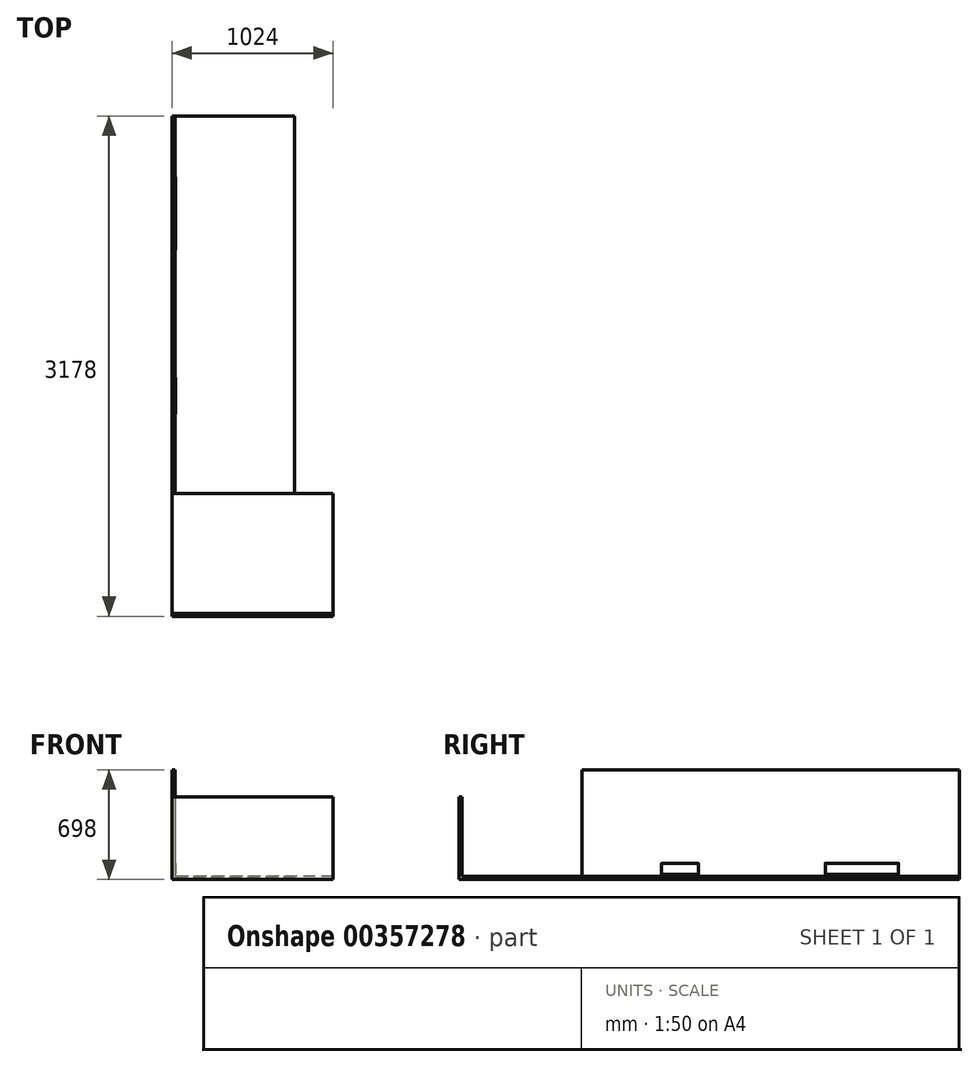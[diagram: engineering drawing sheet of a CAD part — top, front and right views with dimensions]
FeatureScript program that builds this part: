
annotation { "Feature Type Name" : "Feature", "Feature Type Description" : "" }
export const myFeature = defineFeature(function(context is Context, id is Id, definition is map)
    precondition{}
    {
        {
            var Q0;
            Q0=qCreatedBy(makeId("Front.planeOp"),FACE);
            var sketch = newSketch(context, id + "F0", { "sketchPlane" : qUnion([Q0])});
            skLineSegment(sketch, "E0.top", {"start": v(-380, -339.5) * mm, "end": v(380, -339.5) * mm});
            skLineSegment(sketch, "E0.left", {"start": v(-380, 339.5) * mm, "end": v(-380, -339.5) * mm});
            skPoint(sketch, "E0.middle", {"position": v(0, 0) * mm});
            skPoint(sketch, "E0.right.start.orphan", {"position": v(380, 339.5) * mm});
            skLineSegment(sketch, "E1", {"start": v(-380, 339.5) * mm, "end": v(380, -339.5) * mm, "construction": true});
            skLineSegment(sketch, "E2.0", {"start": v(-399, -358.5) * mm, "end": v(380.02, -358.5) * mm});
            skLineSegment(sketch, "E2.1", {"start": v(-399, 339.48) * mm, "end": v(-399, -358.5) * mm});
            skLineSegment(sketch, "E3", {"start": v(-380, 339.5) * mm, "end": v(-399, 339.48) * mm});
            skLineSegment(sketch, "E4", {"start": v(380.02, -358.5) * mm, "end": v(380, -339.5) * mm});
            skSolve(sketch);
        }
        {
            var Q0;
            Q0 = qSketchRegion(id + "F0", true);
            extrude(context, id + "F1", {"entities" : qUnion([Q0]), "endBound" : BoundingType.SYMMETRIC, "depth" : 2398 * mm});
        }
        {
            var Q0;
            Q0=makeQuery(id+"F1.opExtrude","SWEPT_FACE",FACE,{"disambiguationData":[OSD([sQuery(id+"F0.wireOp",EDGE,"E0.left")])]});
            var sketch = newSketch(context, id + "F2", { "sketchPlane" : qUnion([Q0])});
            skLineSegment(sketch, "E5.bottom", {"start": v(-694, -254.5) * mm, "end": v(-461, -254.5) * mm});
            skLineSegment(sketch, "E5.top", {"start": v(-694, -324.5) * mm, "end": v(-461, -324.5) * mm});
            skLineSegment(sketch, "E5.left", {"start": v(-694, -254.5) * mm, "end": v(-694, -324.5) * mm});
            skLineSegment(sketch, "E5.right", {"start": v(-461, -254.5) * mm, "end": v(-461, -324.5) * mm});
            skLineSegment(sketch, "E6.bottom", {"start": v(811, -254.5) * mm, "end": v(346, -254.5) * mm});
            skLineSegment(sketch, "E6.top", {"start": v(811, -324.5) * mm, "end": v(346, -324.5) * mm});
            skLineSegment(sketch, "E6.left", {"start": v(811, -254.5) * mm, "end": v(811, -324.5) * mm});
            skLineSegment(sketch, "E6.right", {"start": v(346, -254.5) * mm, "end": v(346, -324.5) * mm});
            skSolve(sketch);
        }
        {
            var Q0;
            Q0 = qSketchRegion(id + "F2", true);
            extrude(context, id + "F3", {"entities" : qUnion([Q0]), "operationType" : NewBodyOperationType.ADD, "depth" : 5 * mm});
        }
        {
            var Q0;
            Q0=makeQuery(id+"F3.opExtrude","CAP_FACE",FACE,{"disambiguationData":[OSD([sQuery(id+"F2.wireOp",EDGE,"E5.bottom"),sQuery(id+"F2.wireOp",EDGE,"E5.top"),sQuery(id+"F2.wireOp",EDGE,"E5.left"),sQuery(id+"F2.wireOp",EDGE,"E5.right")])],"isStart":false});
            var Q1;
            Q1=makeQuery(id+"F3.opExtrude","CAP_FACE",FACE,{"disambiguationData":[OSD([sQuery(id+"F2.wireOp",EDGE,"E6.bottom"),sQuery(id+"F2.wireOp",EDGE,"E6.top"),sQuery(id+"F2.wireOp",EDGE,"E6.left"),sQuery(id+"F2.wireOp",EDGE,"E6.right")])],"isStart":false});
            fillet(context, id + "F4", {"entities" : qUnion([Q0, Q1]), "radius" : 5 * mm, "tangentPropagation" : true, "allowEdgeOverflow" : false});
        }
        {
            var Q0;
            Q0=makeQuery(id+"F1.opExtrude","SWEPT_FACE",FACE,{"disambiguationData":[OSD([sQuery(id+"F0.wireOp",EDGE,"E2.1")])]});
            var sketch = newSketch(context, id + "F5", { "sketchPlane" : qUnion([Q0])});
            skLineSegment(sketch, "E7", {"start": v(1960, 165.5) * mm, "end": v(1960, -339.5) * mm});
            skLineSegment(sketch, "E8", {"start": v(1960, -339.5) * mm, "end": v(1200, -339.5) * mm});
            skLineSegment(sketch, "E9", {"start": v(1198.4, -339.5) * mm, "end": v(1199.78, -339.5) * mm, "construction": true});
            skLineSegment(sketch, "E10.0", {"start": v(1979, -358.5) * mm, "end": v(1200, -358.5) * mm});
            skLineSegment(sketch, "E10.1", {"start": v(1979, 165.5) * mm, "end": v(1979, -358.5) * mm});
            skLineSegment(sketch, "E11", {"start": v(1960, 165.5) * mm, "end": v(1979, 165.5) * mm});
            skLineSegment(sketch, "E12", {"start": v(1200, -339.5) * mm, "end": v(1200, -358.5) * mm});
            skSolve(sketch);
        }
        {
            var Q0;
            Q0 = qSketchRegion(id + "F5", true);
            extrude(context, id + "F6", {"entities" : qUnion([Q0]), "oppositeDirection" : true, "depth" : 1024 * mm});
        }
    });
